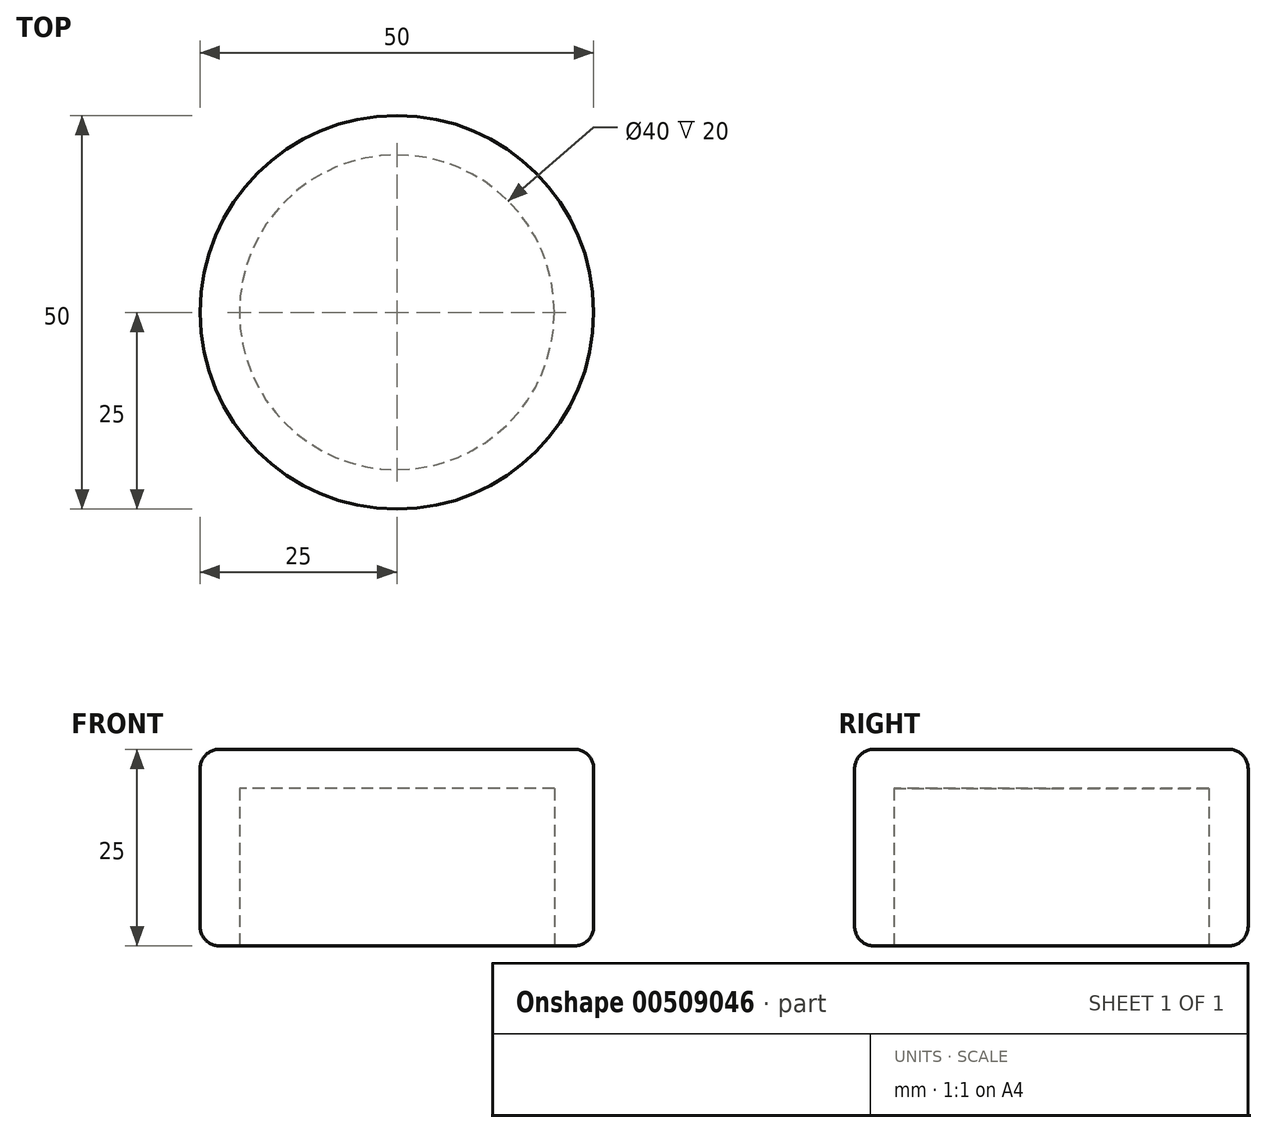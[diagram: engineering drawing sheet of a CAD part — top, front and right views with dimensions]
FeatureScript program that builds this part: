
annotation { "Feature Type Name" : "Feature", "Feature Type Description" : "" }
export const myFeature = defineFeature(function(context is Context, id is Id, definition is map)
    precondition{}
    {
        {
            var Q0;
            Q0=qCreatedBy(makeId("Top.planeOp"),FACE);
            var sketch = newSketch(context, id + "F0", { "sketchPlane" : qUnion([Q0])});
            skCircle(sketch, "E0", {"center": v(0, 0) * mm, "radius": 25 * mm});
            skSolve(sketch);
        }
        {
            var Q0;
            Q0=makeQuery(id+"F0.imprint","IMPRINT",FACE,{"disambiguationData":[TD([[makeQuery(id+"F0.imprint","IMPRINT",EDGE,{"derivedFrom":sQuery(id+"F0.wireOp",EDGE,"E0")}),1.0]])]});
            extrude(context, id + "F1", {"entities" : qUnion([Q0]), "depth" : 25 * mm});
        }
        {
            var Q0;
            Q0=makeQuery(id+"F1.opExtrude","CAP_FACE",FACE,{"disambiguationData":[OSD([sQuery(id+"F0.wireOp",EDGE,"E0")])],"isStart":true});
            shell(context, id + "F2", {"entities" : qUnion([Q0]), "thickness" : 5 * mm});
        }
        {
            var Q0;
            Q0=makeQuery(id+"F1.opExtrude","CAP_EDGE",EDGE,{"disambiguationData":[OSD([sQuery(id+"F0.wireOp",EDGE,"E0")])],"isStart":false});
            fillet(context, id + "F3", {"entities" : qUnion([Q0]), "radius" : 2.5 * mm, "tangentPropagation" : true, "allowEdgeOverflow" : false});
        }
        {
            var Q0;
            Q0=makeQuery(id+"F1.opExtrude","CAP_EDGE",EDGE,{"disambiguationData":[OSD([sQuery(id+"F0.wireOp",EDGE,"E0")])],"isStart":true});
            fillet(context, id + "F4", {"entities" : qUnion([Q0]), "radius" : 2.5 * mm, "tangentPropagation" : true, "allowEdgeOverflow" : false});
        }
    });
